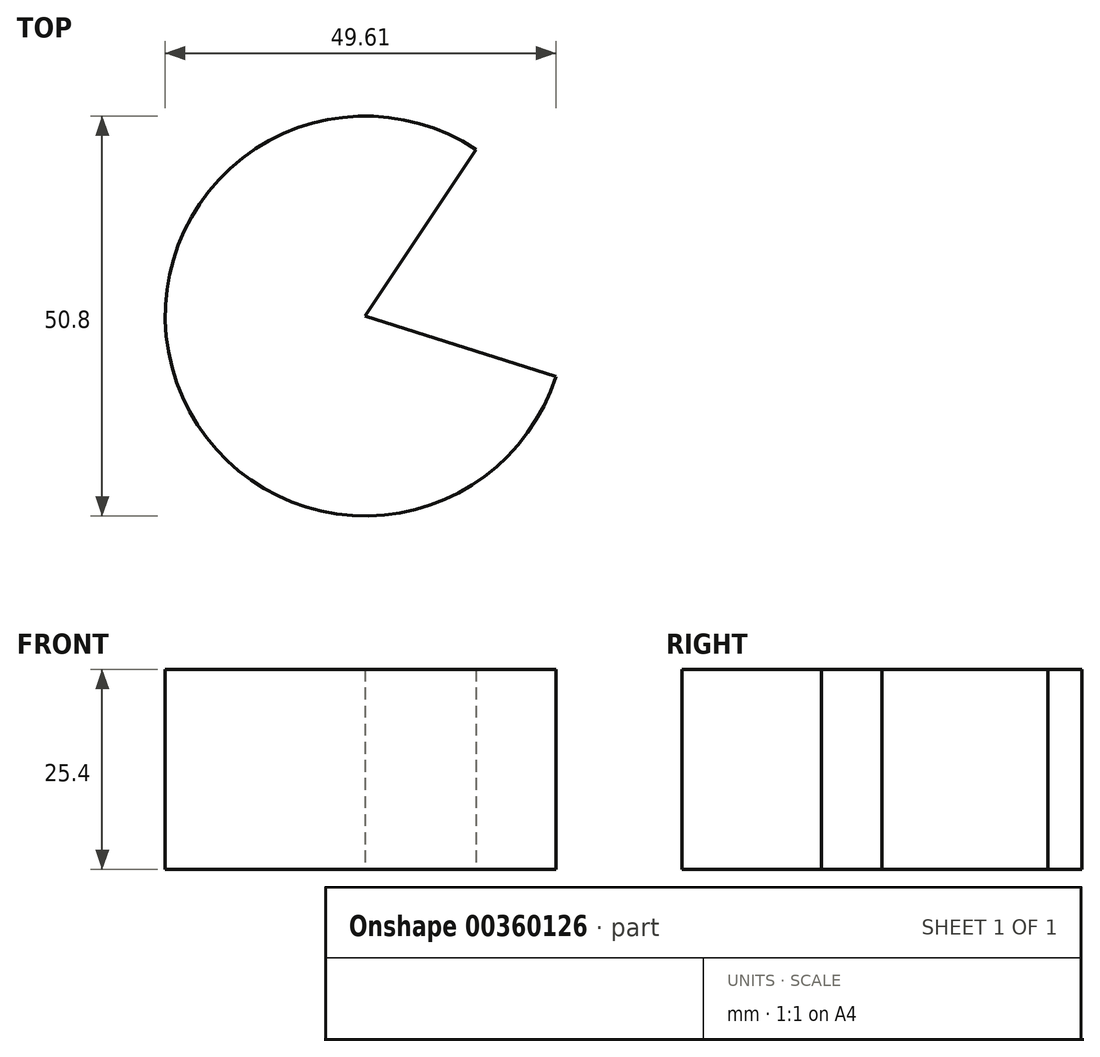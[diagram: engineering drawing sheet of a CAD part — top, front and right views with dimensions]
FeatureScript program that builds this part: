
annotation { "Feature Type Name" : "Feature", "Feature Type Description" : "" }
export const myFeature = defineFeature(function(context is Context, id is Id, definition is map)
    precondition{}
    {
        {
            var Q0;
            Q0=qCreatedBy(makeId("Top.planeOp"),FACE);
            var sketch = newSketch(context, id + "F0", { "sketchPlane" : qUnion([Q0])});
            skLineSegment(sketch, "E0", {"start": v(50.8, 0) * mm, "end": v(26.65, 0) * mm});
            skLineSegment(sketch, "E1", {"start": v(50.8, 76.2) * mm, "end": v(50.8, 0) * mm});
            skLineSegment(sketch, "E2", {"start": v(50.8, 76.2) * mm, "end": v(0, 0) * mm});
            skCircle(sketch, "E3", {"center": v(0, 0) * mm, "radius": 25.4 * mm});
            skLineSegment(sketch, "E4", {"start": v(50.8, 76.2) * mm, "end": v(24.21, -7.68) * mm});
            skLineSegment(sketch, "E5", {"start": v(0, 0) * mm, "end": v(24.21, -7.68) * mm});
            skLineSegment(sketch, "E6", {"start": v(50.8, 20.9) * mm, "end": v(50.8, 76.2) * mm});
            skSolve(sketch);
        }
        {
            var Q0;
            {var subQ0=sQuery(id+"F0.wireOp",EDGE,"E5");Q0=makeQuery(id+"F0.imprint","IMPRINT",FACE,{"disambiguationData":[TD([[makeQuery(id+"F0.imprint","IMPRINT",EDGE,{"derivedFrom":subQ0}),-1.0]])]});}
            extrude(context, id + "F1", {"entities" : qUnion([Q0]), "depth" : 25.4 * mm});
        }
    });
